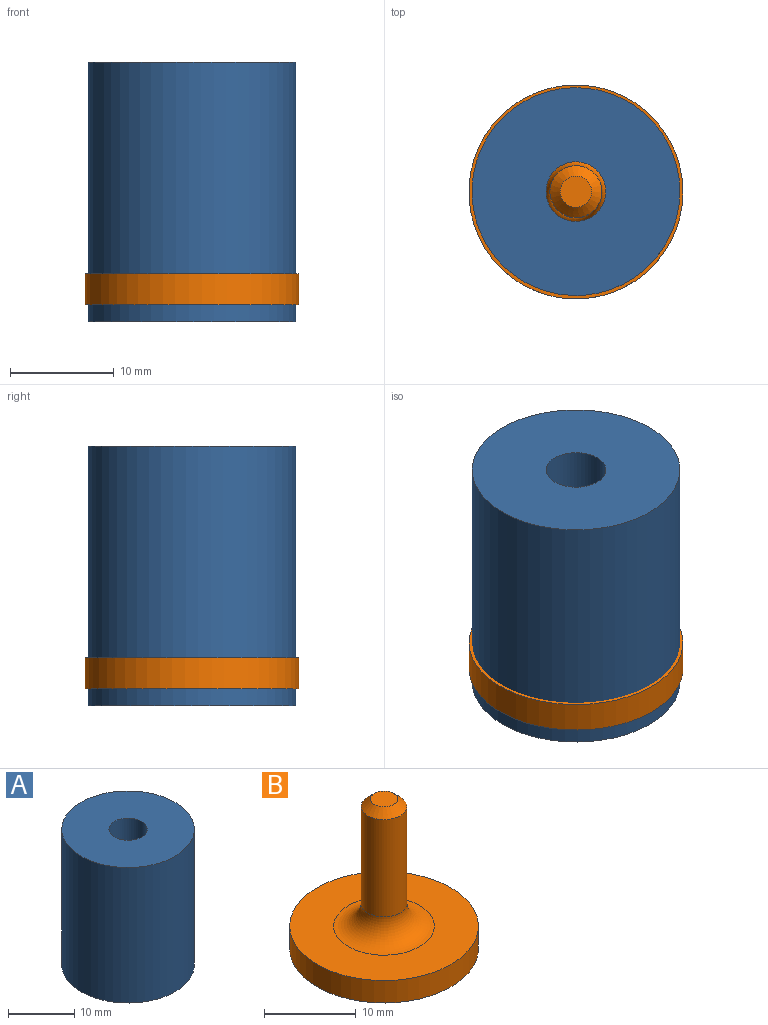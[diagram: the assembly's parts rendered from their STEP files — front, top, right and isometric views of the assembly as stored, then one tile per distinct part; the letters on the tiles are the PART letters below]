
ASSEMBLY  parts=2 mates=1
PART A: 5 faces, bbox 20x20x25 mm
  f0: cylinder r=2.88mm len=21.75mm, axis (0,0,-1), area 392.9mm2, adj f2,f4
  f1: cylinder r=10mm len=25mm, axis (0,0,-1), area 1570.8mm2, adj f2,f3
  f2: plane 20x20mm, normal (0,0,1), area 288.2mm2, adj f0,f1
  f3: plane 20x20mm, normal (0,0,-1), area 196.3mm2, adj f1,f4
  f4: torus R=6.12mm, axis (0,0,1), area 130.1mm2, adj f0,f3
PART B: 7 faces, bbox 20.6x20.6x20 mm
  f0: cylinder r=10.3mm len=20.6mm, axis (0,0,-1), area 194.2mm2, adj f1,f2
  f1: plane 20.6x20.6mm, normal (0,0,1), area 238.3mm2, adj f0,f5
  f2: plane 20.6x20.6mm, normal (0,0,-1), area 333.3mm2, adj f0
  f3: cylinder r=2.5mm len=13mm, axis (0,0,-1), area 204.2mm2, adj f5,f6
  f4: plane 3x3mm, normal (0,0,1), area 7.1mm2, adj f6
  f5: torus R=5.5mm, axis (0,0,1), area 106.3mm2, adj f1,f3
  f6: cone r=1.5mm half-angle=45deg, axis (0,0,-1), area 17.8mm2, adj f3,f4
PLACE A rot(axis=(-0.52,0.61,0.6),0deg) t=(-18.61,16.29,-17.95)mm
PLACE B rot(axis=(-0.52,0.61,0.6),0deg) t=(-18.61,16.29,-16.33)mm
MATE slider A.f0 <-> B.f3  axis (0,0,-1) through (-18.61,16.29,-3.83)mm
